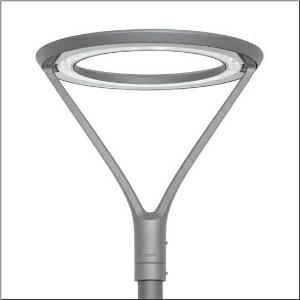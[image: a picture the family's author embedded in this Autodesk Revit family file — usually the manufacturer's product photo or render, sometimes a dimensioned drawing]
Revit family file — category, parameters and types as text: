
# Revit family: dl_20___pl1_2s_5xa512832s008p_db7a
name_source: partatom
category: Lighting Fixtures
units: mm (PartAtom-declared; Revit-internal decimal feet)

## family parameters
Cut with Voids When Loaded = No
Host = Face
Light Source = No
Part Type = Normal
Room Calculation Point = No
Round Connector Dimension = Use Diameter
Shared = No

## types (1)
- --- (1 x LED, 4250 lm, 43.6 W, 2200K)
    Apparent Load = 44 VA
    CIE Flux Codes = 33 78 99 100 100
    Color Rendering = 70
    Color Temperature = 2200K
    Default Elevation = 1800 mm
    Description = DL® 20, mast luminaire, primary light control with reflector, highly specular, primary optical cover: cover, of toughened safety glass of clear glass with excellent transmission level, light distribution: PL1.2s, light emission: direct distribution, primary light characteristic: symmetric, installation type: post-top, LED, High Power LED, rated luminous flux: 4.210lm, luminous efficacy: 80lm/W, light colour: 722, colour temperature: 2200K, control gear: Plus, control: flexible luminous flux parameterisation, time-dependent luminous flux control, constant luminous flux control, digital communication interface, power reduction, overheat protection, electronic power reduction, mains connection: 230..240V, 50/60Hz, connection cable pre-assembled, cable length: 5m, start of lifetime: 53W, end of service life: 54W, reduction: 24W, luminaire housing, upper part, of cast aluminium, powder-coated, Siteco® metallic grey (DB 702S), diameter: 690mm, height: 690mm, spigot size: 76mm (post-top), mounting height: 4..6m, luminaire housing, of cast aluminium, powder-coated, Siteco® metallic grey (DB 702S), equipment: Power, protection rating (complete): IP66, insulation class (complete): insulation class II (safety insulation), certification: CE, ENEC, VDE, impact resistance: IK08, permissible operating ambient temperature: -25..+30°C, standard-compliant lighting for roads and squares, packaging unit: 1 piece

Light Distribution: PL1.2s
    Height = 690 mm
    Lamp = 1 x LED
    Lamp Light Flux = 4250 lm
    Lamp Power = 43.6 W
    Lamp count = 1
    Length = 690 mm
    Luminous efficacy = 97 lm/W
    Manufacturer = Siteco
    ModVariant = No
    Model = 5XA512832S008P
    Number of Poles = 1
    OnlyDefault = Yes
    Power Factor = 1
    Product Name = DL 20 | PL1.2s
    Product group = mast luminaire | pylon top
    ProductGroupID = 6100
    Protection Class = Protection class II
    Protection Degree = IP 66
    RLX_Detail_Level = 1
    RLX_Emergency_Light_Flux = 0 lm
    RLX_Emergency_Type = 0
    RLX_Emergency_Type_DB = No
    RlxData = <blob elided: 204313 chars, md5=a9427a16>
    Socket = socket
    Standby Power = 0 W
    System Light Flux = 4250 lm
    System Power = 44 W
    Type Comments = factory setting: luminous flux: 100 % | dim-lin: 254 | 587 mA
    Type Image = l_1006001.jpg
    URL = http://relux.com
    VarID = @adj_084709
    Voltage = 0 V
    Weight = 0.00 kg
    Width = 0 mm  [stored 0 ft]

note: [stored X ft] marks values corroborated as IEEE doubles in the binary element streams (Revit-internal decimal feet)

## geometry (parser evidence)
native form markers: Blend x4, Sweep x10
no freeform markers — native parametric forms only
